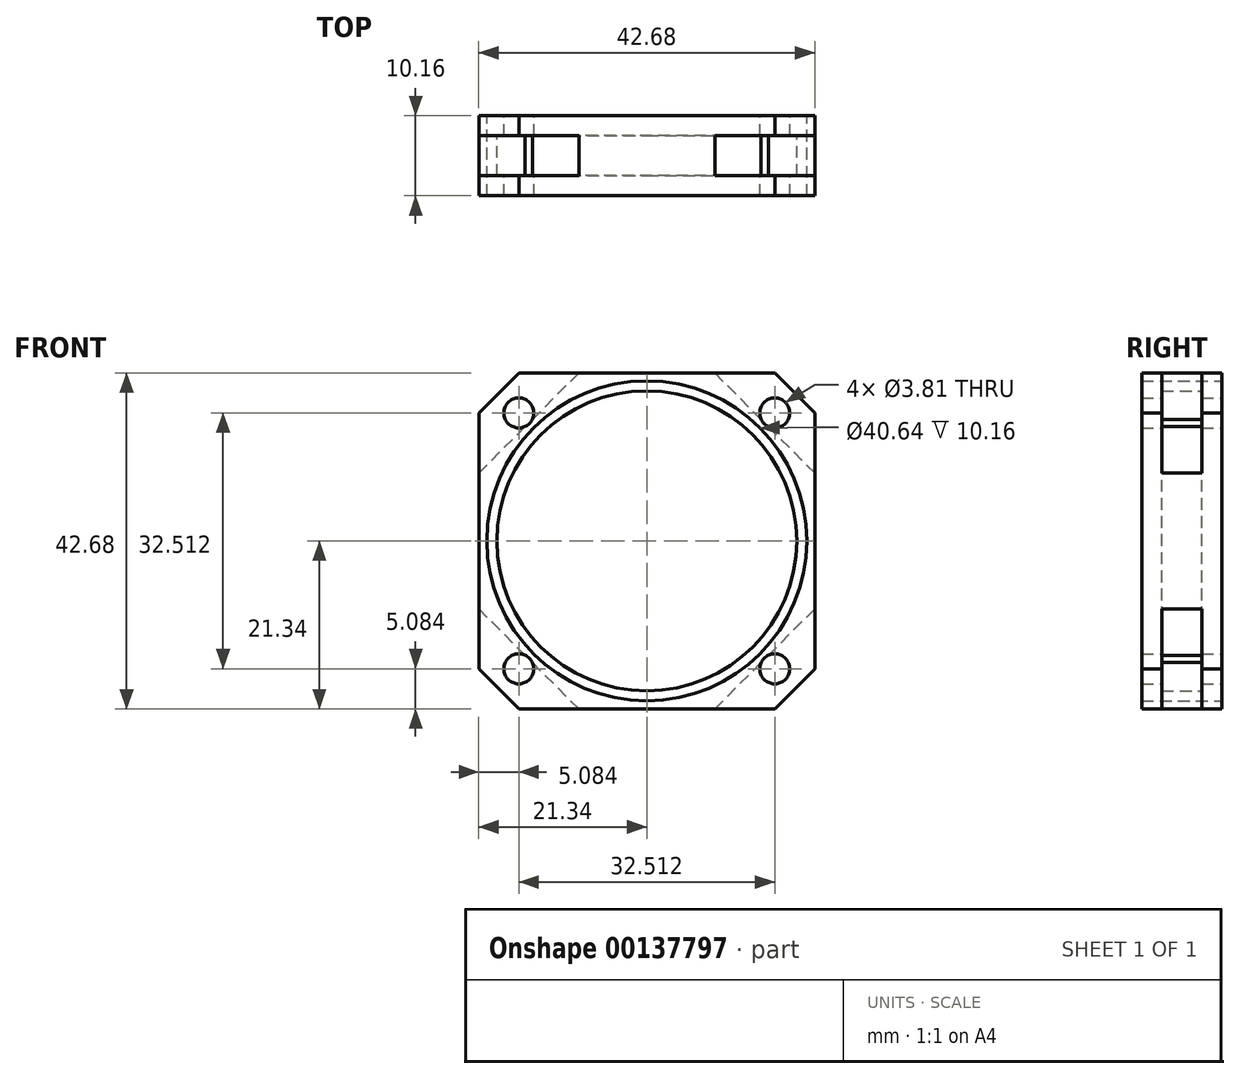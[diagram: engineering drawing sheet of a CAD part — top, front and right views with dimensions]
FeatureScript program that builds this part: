
annotation { "Feature Type Name" : "Feature", "Feature Type Description" : "" }
export const myFeature = defineFeature(function(context is Context, id is Id, definition is map)
    precondition{}
    {
        {
            var Q0;
            Q0=qCreatedBy(makeId("Front.planeOp"),FACE);
            var sketch = newSketch(context, id + "F0", { "sketchPlane" : qUnion([Q0])});
            skLineSegment(sketch, "E0.bottom", {"start": v(-21.34, 21.34) * mm, "end": v(21.34, 21.34) * mm});
            skLineSegment(sketch, "E0.top", {"start": v(-21.34, -21.34) * mm, "end": v(21.34, -21.34) * mm});
            skLineSegment(sketch, "E0.left", {"start": v(-21.34, 21.34) * mm, "end": v(-21.34, -21.34) * mm});
            skLineSegment(sketch, "E0.right", {"start": v(21.34, 21.34) * mm, "end": v(21.34, -21.34) * mm});
            skPoint(sketch, "E0.middle", {"position": v(0, 0) * mm});
            skCircle(sketch, "E1", {"center": v(0, 0) * mm, "radius": 20.32 * mm});
            skCircle(sketch, "E2", {"center": v(-16.26, 16.26) * mm, "radius": 1.9 * mm});
            skCircle(sketch, "E3", {"center": v(16.26, 16.26) * mm, "radius": 1.9 * mm});
            skCircle(sketch, "E4", {"center": v(16.26, -16.26) * mm, "radius": 1.9 * mm});
            skCircle(sketch, "E5", {"center": v(-16.26, -16.26) * mm, "radius": 1.9 * mm});
            skCircle(sketch, "E6", {"center": v(0, 0) * mm, "radius": 19.05 * mm});
            skLineSegment(sketch, "E7", {"start": v(-8.64, 21.34) * mm, "end": v(-21.34, 8.64) * mm});
            skLineSegment(sketch, "E8", {"start": v(-21.34, -8.64) * mm, "end": v(-8.64, -21.34) * mm});
            skLineSegment(sketch, "E9", {"start": v(8.64, 21.34) * mm, "end": v(21.34, 8.64) * mm});
            skLineSegment(sketch, "E10", {"start": v(21.34, -8.64) * mm, "end": v(8.64, -21.34) * mm});
            skSolve(sketch);
        }
        {
            var Q0;
            Q0=makeQuery(id+"F0.imprint","IMPRINT",FACE,{"disambiguationData":[TD([[makeQuery(id+"F0.imprint","IMPRINT",EDGE,{"derivedFrom":sQuery(id+"F0.wireOp",EDGE,"E0.bottom")}),-1.0]])]});
            var Q1;
            Q1=makeQuery(id+"F0.imprint","IMPRINT",FACE,{"disambiguationData":[TD([[makeQuery(id+"F0.imprint","IMPRINT",EDGE,{"derivedFrom":sQuery(id+"F0.wireOp",EDGE,"E1")}),-1.0]])]});
            var Q2;
            {var subQ1=sQuery(id+"F0.wireOp",EDGE,"E0.right");var subQ6=sQuery(id+"F0.wireOp",EDGE,"E0.top");var subQ7=makeQuery(id+"F0.imprint","INTERSECT",VERTEX,{"derivedFrom":[subQ6,subQ1]});Q2=makeQuery(id+"F0.imprint","IMPRINT",FACE,{"disambiguationData":[TD([[makeQuery(id+"F0.imprint","IMPRINT",EDGE,{"disambiguationData":[TD([[subQ7,1.0]])],"derivedFrom":subQ6}),1.0]])]});}
            var Q3;
            {var subQ4=sQuery(id+"F0.wireOp",EDGE,"E0.top");var subQ6=sQuery(id+"F0.wireOp",EDGE,"E0.left");var subQ8=makeQuery(id+"F0.imprint","INTERSECT",VERTEX,{"derivedFrom":[subQ4,subQ6]});Q3=makeQuery(id+"F0.imprint","IMPRINT",FACE,{"disambiguationData":[TD([[makeQuery(id+"F0.imprint","IMPRINT",EDGE,{"disambiguationData":[TD([[subQ8,-1.0]])],"derivedFrom":subQ4}),1.0]])]});}
            extrude(context, id + "F1", {"entities" : qUnion([Q0, Q1, Q2, Q3]), "endBound" : BoundingType.SYMMETRIC, "depth" : 10.16 * mm});
        }
        {
            var Q0;
            Q0=makeQuery(id+"F1.opExtrude","SWEPT_EDGE",EDGE,{"disambiguationData":[OSD([sQuery(id+"F0.wireOp",EDGE,"E0.bottom"),sQuery(id+"F0.wireOp",EDGE,"E0.left")])]});
            var Q1;
            Q1=makeQuery(id+"F1.opExtrude","SWEPT_EDGE",EDGE,{"disambiguationData":[OSD([sQuery(id+"F0.wireOp",EDGE,"E0.top"),sQuery(id+"F0.wireOp",EDGE,"E0.left")])]});
            var Q2;
            Q2=makeQuery(id+"F1.opExtrude","SWEPT_EDGE",EDGE,{"disambiguationData":[OSD([sQuery(id+"F0.wireOp",EDGE,"E0.top"),sQuery(id+"F0.wireOp",EDGE,"E0.right")])]});
            var Q3;
            Q3=makeQuery(id+"F1.opExtrude","SWEPT_EDGE",EDGE,{"disambiguationData":[OSD([sQuery(id+"F0.wireOp",EDGE,"E0.bottom"),sQuery(id+"F0.wireOp",EDGE,"E0.right")])]});
            chamfer(context, id + "F2", {"entities" : qUnion([Q0, Q1, Q2, Q3]), "width" : 5.08 * mm, "tangentPropagation" : true});
        }
        {
            var Q0;
            {var subQ4=sQuery(id+"F0.wireOp",EDGE,"E0.bottom");var subQ6=sQuery(id+"F0.wireOp",EDGE,"E0.left");var subQ7=makeQuery(id+"F0.imprint","INTERSECT",VERTEX,{"derivedFrom":[subQ4,subQ6]});Q0=makeQuery(id+"F0.imprint","IMPRINT",FACE,{"disambiguationData":[TD([[makeQuery(id+"F0.imprint","IMPRINT",EDGE,{"disambiguationData":[TD([[subQ7,-1.0]])],"derivedFrom":subQ4}),-1.0]])]});}
            var Q1;
            {var subQ1=sQuery(id+"F0.wireOp",EDGE,"E0.bottom");var subQ5=sQuery(id+"F0.wireOp",EDGE,"E0.right");var subQ6=makeQuery(id+"F0.imprint","INTERSECT",VERTEX,{"derivedFrom":[subQ1,subQ5]});Q1=makeQuery(id+"F0.imprint","IMPRINT",FACE,{"disambiguationData":[TD([[makeQuery(id+"F0.imprint","IMPRINT",EDGE,{"disambiguationData":[TD([[subQ6,1.0]])],"derivedFrom":subQ1}),-1.0]])]});}
            var Q2;
            {var subQ1=sQuery(id+"F0.wireOp",EDGE,"E0.right");var subQ6=sQuery(id+"F0.wireOp",EDGE,"E0.top");var subQ7=makeQuery(id+"F0.imprint","INTERSECT",VERTEX,{"derivedFrom":[subQ6,subQ1]});Q2=makeQuery(id+"F0.imprint","IMPRINT",FACE,{"disambiguationData":[TD([[makeQuery(id+"F0.imprint","IMPRINT",EDGE,{"disambiguationData":[TD([[subQ7,1.0]])],"derivedFrom":subQ6}),1.0]])]});}
            var Q3;
            {var subQ4=sQuery(id+"F0.wireOp",EDGE,"E0.top");var subQ6=sQuery(id+"F0.wireOp",EDGE,"E0.left");var subQ8=makeQuery(id+"F0.imprint","INTERSECT",VERTEX,{"derivedFrom":[subQ4,subQ6]});Q3=makeQuery(id+"F0.imprint","IMPRINT",FACE,{"disambiguationData":[TD([[makeQuery(id+"F0.imprint","IMPRINT",EDGE,{"disambiguationData":[TD([[subQ8,-1.0]])],"derivedFrom":subQ4}),1.0]])]});}
            extrude(context, id + "F3", {"entities" : qUnion([Q0, Q1, Q2, Q3]), "operationType" : NewBodyOperationType.REMOVE, "endBound" : BoundingType.SYMMETRIC, "oppositeDirection" : true, "depth" : 5.08 * mm});
        }
        {
            var Q0;
            Q0=makeQuery(id+"F0.imprint","IMPRINT",FACE,{"disambiguationData":[TD([[makeQuery(id+"F0.imprint","IMPRINT",EDGE,{"derivedFrom":sQuery(id+"F0.wireOp",EDGE,"E6")}),1.0]])]});
            extrude(context, id + "F4", {"entities" : qUnion([Q0]), "operationType" : NewBodyOperationType.ADD, "endBound" : BoundingType.SYMMETRIC, "depth" : 5.08 * mm});
        }
    });
